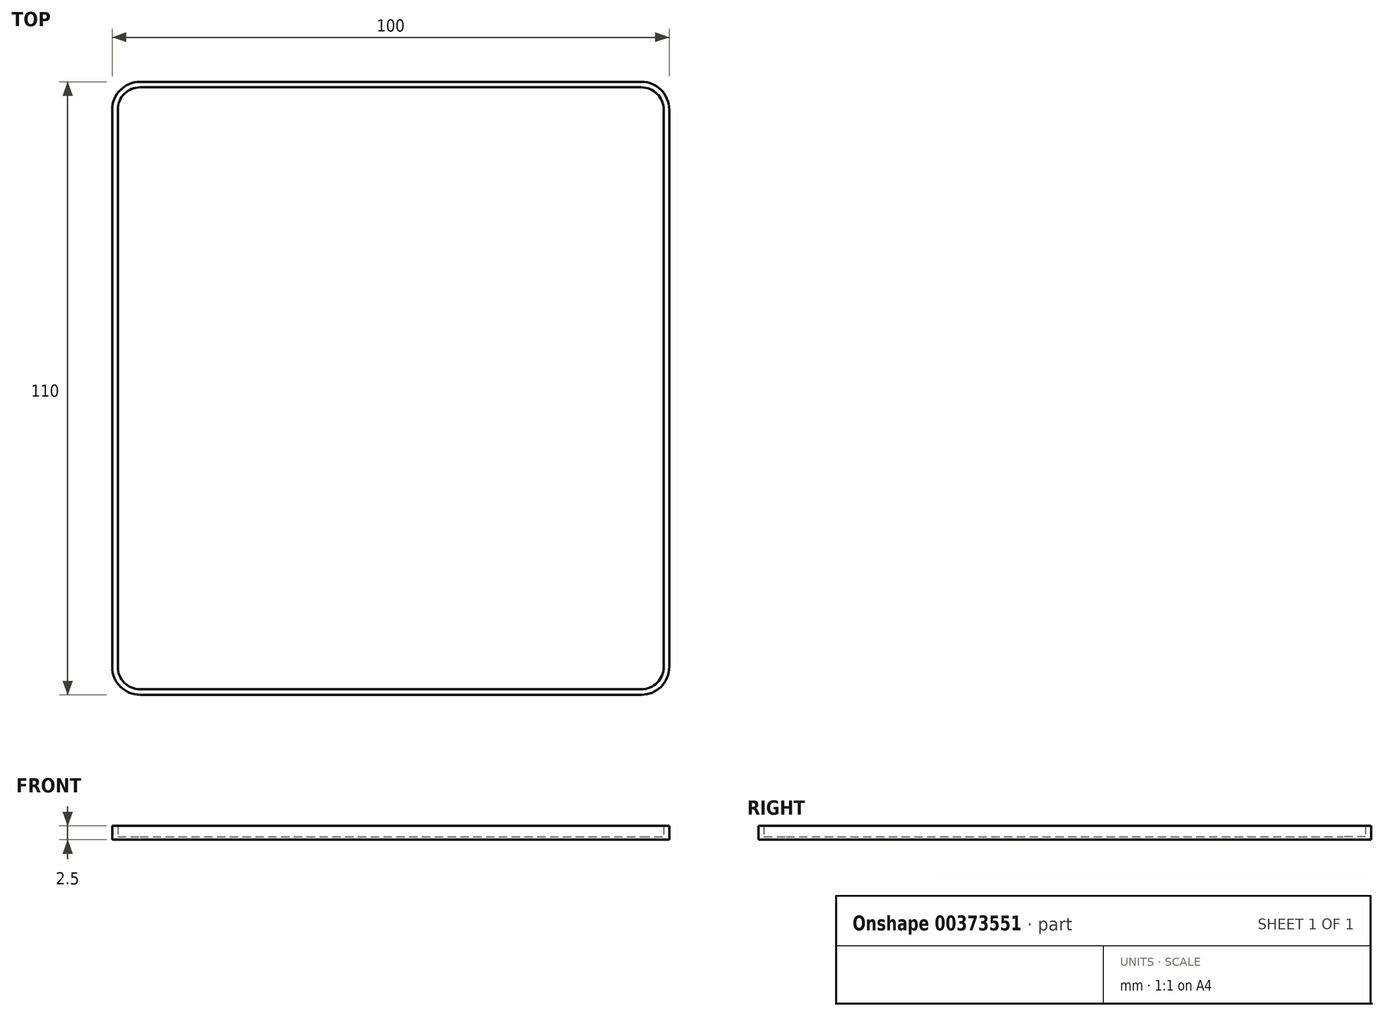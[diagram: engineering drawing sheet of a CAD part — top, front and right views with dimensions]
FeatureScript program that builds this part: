
annotation { "Feature Type Name" : "Feature", "Feature Type Description" : "" }
export const myFeature = defineFeature(function(context is Context, id is Id, definition is map)
    precondition{}
    {
        {
            var Q0;
            Q0=qCreatedBy(makeId("Top.planeOp"),FACE);
            var sketch = newSketch(context, id + "F0", { "sketchPlane" : qUnion([Q0])});
            skLineSegment(sketch, "E0.bottom", {"start": v(45, -53.92) * mm, "end": v(-45, -53.92) * mm});
            skLineSegment(sketch, "E0.top", {"start": v(45, 56.08) * mm, "end": v(-45, 56.08) * mm});
            skLineSegment(sketch, "E0.left", {"start": v(50, -48.92) * mm, "end": v(50, 51.08) * mm});
            skLineSegment(sketch, "E0.right", {"start": v(-50, -48.92) * mm, "end": v(-50, 51.08) * mm});
            skPoint(sketch, "E0.middle", {"position": v(0, 1.08) * mm});
            skPoint(sketch, "E1.visualSharp", {"position": v(-50, 56.08) * mm});
            skArc(sketch, "E1.filletArc", {"start": v(-45, 56.08) * mm, "mid": v(-48.54, 54.62) * mm, "end": v(-50, 51.08) * mm});
            skPoint(sketch, "E2.visualSharp", {"position": v(50, 56.08) * mm});
            skArc(sketch, "E2.filletArc", {"start": v(50, 51.08) * mm, "mid": v(48.54, 54.62) * mm, "end": v(45, 56.08) * mm});
            skPoint(sketch, "E3.visualSharp", {"position": v(50, -53.92) * mm});
            skArc(sketch, "E3.filletArc", {"start": v(45, -53.92) * mm, "mid": v(48.54, -52.45) * mm, "end": v(50, -48.92) * mm});
            skPoint(sketch, "E4.visualSharp", {"position": v(-50, -53.92) * mm});
            skArc(sketch, "E4.filletArc", {"start": v(-50, -48.92) * mm, "mid": v(-48.54, -52.45) * mm, "end": v(-45, -53.92) * mm});
            skSolve(sketch);
        }
        {
            var Q0;
            Q0=makeQuery(id+"F0.imprint","IMPRINT",FACE,{"disambiguationData":[TD([[makeQuery(id+"F0.imprint","IMPRINT",EDGE,{"derivedFrom":sQuery(id+"F0.wireOp",EDGE,"E0.bottom")}),-1.0]])]});
            extrude(context, id + "F1", {"entities" : qUnion([Q0]), "depth" : .5 * mm});
        }
        {
            var Q0;
            Q0=makeQuery(id+"F1.opExtrude","CAP_FACE",FACE,{"disambiguationData":[OSD([sQuery(id+"F0.wireOp",EDGE,"E0.bottom"),sQuery(id+"F0.wireOp",EDGE,"E0.top"),sQuery(id+"F0.wireOp",EDGE,"E0.left"),sQuery(id+"F0.wireOp",EDGE,"E0.right"),sQuery(id+"F0.wireOp",EDGE,"E1.filletArc"),sQuery(id+"F0.wireOp",EDGE,"E2.filletArc"),sQuery(id+"F0.wireOp",EDGE,"E3.filletArc"),sQuery(id+"F0.wireOp",EDGE,"E4.filletArc")])],"isStart":false});
            var sketch = newSketch(context, id + "F2", { "sketchPlane" : qUnion([Q0])});
            skLineSegment(sketch, "E5.0", {"start": v(49, -48.92) * mm, "end": v(49, 51.08) * mm});
            skArc(sketch, "E5.1", {"start": v(45, -52.92) * mm, "mid": v(47.83, -51.75) * mm, "end": v(49, -48.92) * mm});
            skArc(sketch, "E5.2", {"start": v(49, 51.08) * mm, "mid": v(47.83, 53.91) * mm, "end": v(45, 55.08) * mm});
            skLineSegment(sketch, "E5.3", {"start": v(-45, -52.92) * mm, "end": v(45, -52.92) * mm});
            skLineSegment(sketch, "E5.4", {"start": v(45, 55.08) * mm, "end": v(-45, 55.08) * mm});
            skArc(sketch, "E5.5", {"start": v(-45, 55.08) * mm, "mid": v(-47.83, 53.91) * mm, "end": v(-49, 51.08) * mm});
            skLineSegment(sketch, "E5.6", {"start": v(-49, 51.08) * mm, "end": v(-49, -48.92) * mm});
            skArc(sketch, "E5.7", {"start": v(-49, -48.92) * mm, "mid": v(-47.83, -51.75) * mm, "end": v(-45, -52.92) * mm});
            skLineSegment(sketch, "E6.0", {"start": v(50, -48.92) * mm, "end": v(50, 51.08) * mm});
            skArc(sketch, "E6.1", {"start": v(45, -53.92) * mm, "mid": v(48.54, -52.45) * mm, "end": v(50, -48.92) * mm});
            skArc(sketch, "E6.2", {"start": v(50, 51.08) * mm, "mid": v(48.54, 54.62) * mm, "end": v(45, 56.08) * mm});
            skLineSegment(sketch, "E6.3", {"start": v(-45, -53.92) * mm, "end": v(45, -53.92) * mm});
            skLineSegment(sketch, "E6.4", {"start": v(45, 56.08) * mm, "end": v(-45, 56.08) * mm});
            skArc(sketch, "E6.5", {"start": v(-45, 56.08) * mm, "mid": v(-48.54, 54.62) * mm, "end": v(-50, 51.08) * mm});
            skLineSegment(sketch, "E6.6", {"start": v(-50, 51.08) * mm, "end": v(-50, -48.92) * mm});
            skArc(sketch, "E6.7", {"start": v(-50, -48.92) * mm, "mid": v(-48.54, -52.45) * mm, "end": v(-45, -53.92) * mm});
            skSolve(sketch);
        }
        {
            var Q0;
            Q0=qSketchRegion(id+"F2",true);
            extrude(context, id + "F3", {"entities" : qUnion([Q0]), "operationType" : NewBodyOperationType.ADD, "depth" : 2 * mm});
        }
    });
